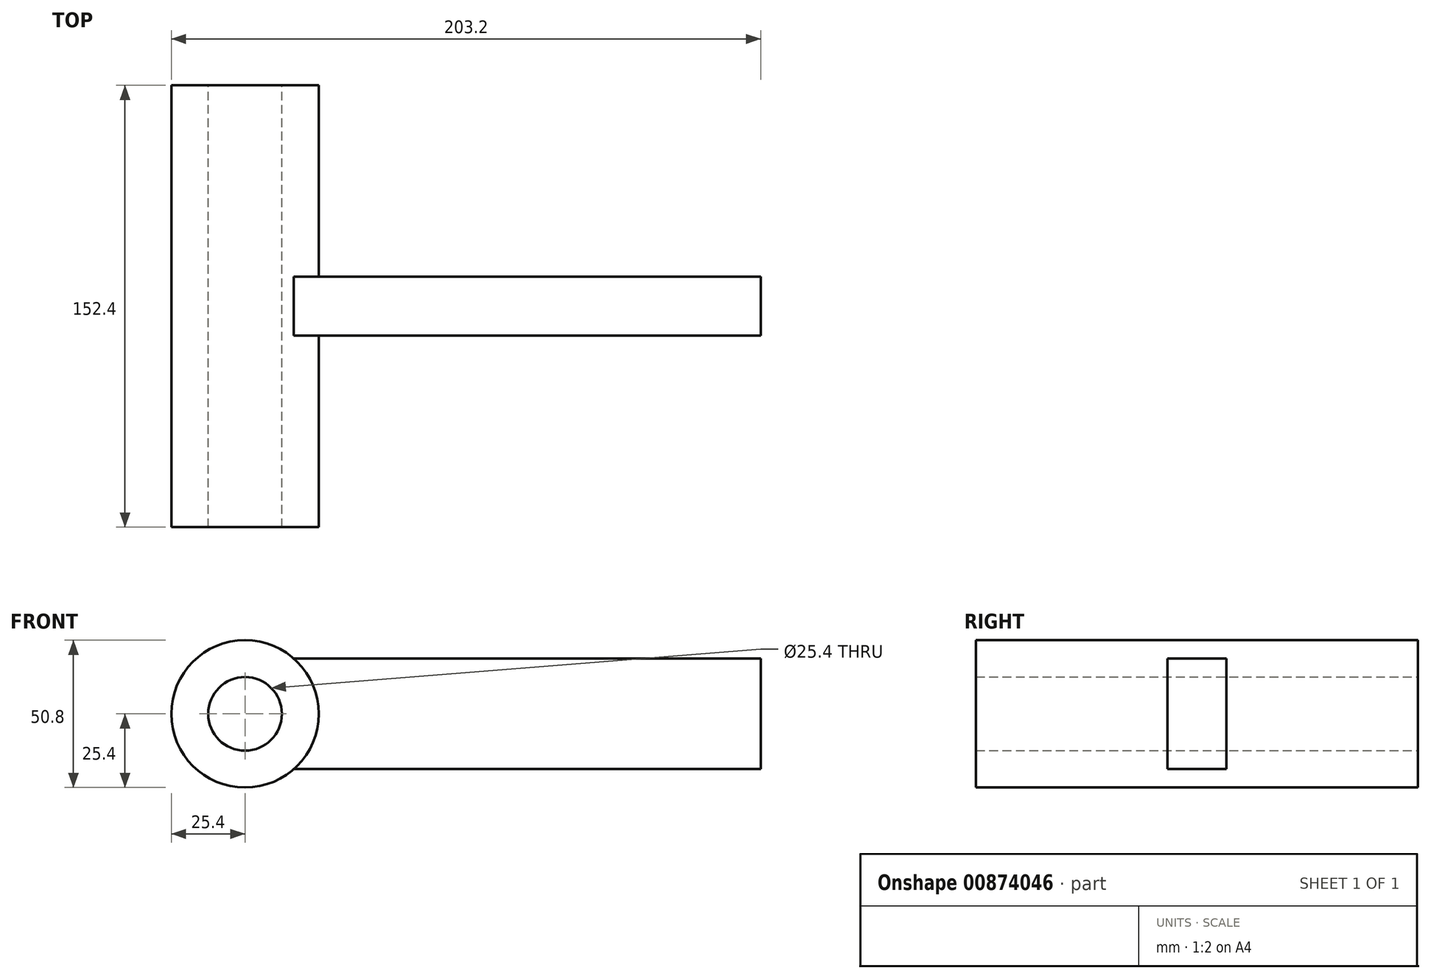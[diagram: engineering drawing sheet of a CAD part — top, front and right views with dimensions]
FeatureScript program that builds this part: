
annotation { "Feature Type Name" : "Feature", "Feature Type Description" : "" }
export const myFeature = defineFeature(function(context is Context, id is Id, definition is map)
    precondition{}
    {
        {
            var Q0;
            Q0=qCreatedBy(makeId("Front.planeOp"),FACE);
            var sketch = newSketch(context, id + "F0", { "sketchPlane" : qUnion([Q0])});
            skCircle(sketch, "E0", {"center": v(0, 0) * mm, "radius": 25.4 * mm});
            skCircle(sketch, "E1", {"center": v(0, 0) * mm, "radius": 12.7 * mm});
            skSolve(sketch);
        }
        {
            var Q0;
            Q0=makeQuery(id+"F0.imprint","IMPRINT",FACE,{"disambiguationData":[TD([[makeQuery(id+"F0.imprint","IMPRINT",EDGE,{"derivedFrom":sQuery(id+"F0.wireOp",EDGE,"E0")}),1.0]])]});
            extrude(context, id + "F1", {"entities" : qUnion([Q0]), "depth" : 76.2 * mm, "offsetDistance" : 25.4 * mm});
        }
        {
            var Q0;
            Q0=makeQuery(id+"F1.opExtrude","CAP_FACE",FACE,{"disambiguationData":[OSD([sQuery(id+"F0.wireOp",EDGE,"E0"),sQuery(id+"F0.wireOp",EDGE,"E1")])],"isStart":true});
            extrude(context, id + "F2", {"entities" : qUnion([Q0]), "operationType" : NewBodyOperationType.ADD, "depth" : 76.2 * mm, "offsetDistance" : 25.4 * mm});
        }
        {
            var Q0;
            Q0=qCreatedBy(makeId("Right.planeOp"),FACE);
            var sketch = newSketch(context, id + "F3", { "sketchPlane" : qUnion([Q0])});
            skLineSegment(sketch, "E2.bottom", {"start": v(-10.16, 19.05) * mm, "end": v(10.16, 19.05) * mm});
            skLineSegment(sketch, "E2.top", {"start": v(-10.16, -19.05) * mm, "end": v(10.16, -19.05) * mm});
            skLineSegment(sketch, "E2.left", {"start": v(-10.16, 19.05) * mm, "end": v(-10.16, -19.05) * mm});
            skLineSegment(sketch, "E2.right", {"start": v(10.16, 19.05) * mm, "end": v(10.16, -19.05) * mm});
            skSolve(sketch);
        }
        {
            var Q0;
            Q0 = qSketchRegion(id + "F3", true);
            extrude(context, id + "F4", {"entities" : qUnion([Q0]), "operationType" : NewBodyOperationType.ADD, "depth" : 177.8 * mm, "offsetDistance" : 25.4 * mm});
        }
        {
            var Q0;
            Q0=sQuery(id+"F0.wireOp",VERTEX,"E0.center");
            var Q1;
            Q1=makeQuery(id+"F1.opExtrude","SWEPT_BODY",BODY,{"disambiguationData":[OSD([sQuery(id+"F0.wireOp",EDGE,"E0"),sQuery(id+"F0.wireOp",EDGE,"E1")])]});
            hole(context, id + "F5", {"style" : HoleStyle.SIMPLE, "endStyle" : HoleEndStyle.THROUGH, "oppositeDirection" : true, "holeDiameter" : 25.4 * mm, "majorDiameter" : 6.35 * mm, "isTappedThrough" : true, "tappedDepth" : 12.7 * mm, "tapClearance" : 3, "locations" : qUnion([Q0]), "scope" : qUnion([Q1])});
        }
        {
            var Q0;
            Q0=sQuery(id+"F0.wireOp",VERTEX,"E0.center");
            var Q1;
            Q1=makeQuery(id+"F1.opExtrude","SWEPT_BODY",BODY,{"disambiguationData":[OSD([sQuery(id+"F0.wireOp",EDGE,"E0"),sQuery(id+"F0.wireOp",EDGE,"E1")])]});
            hole(context, id + "F6", {"style" : HoleStyle.SIMPLE, "endStyle" : HoleEndStyle.THROUGH, "holeDiameter" : 25.4 * mm, "majorDiameter" : 6.35 * mm, "isTappedThrough" : true, "tappedDepth" : 12.7 * mm, "tapClearance" : 3, "locations" : qUnion([Q0]), "scope" : qUnion([Q1])});
        }
    });
